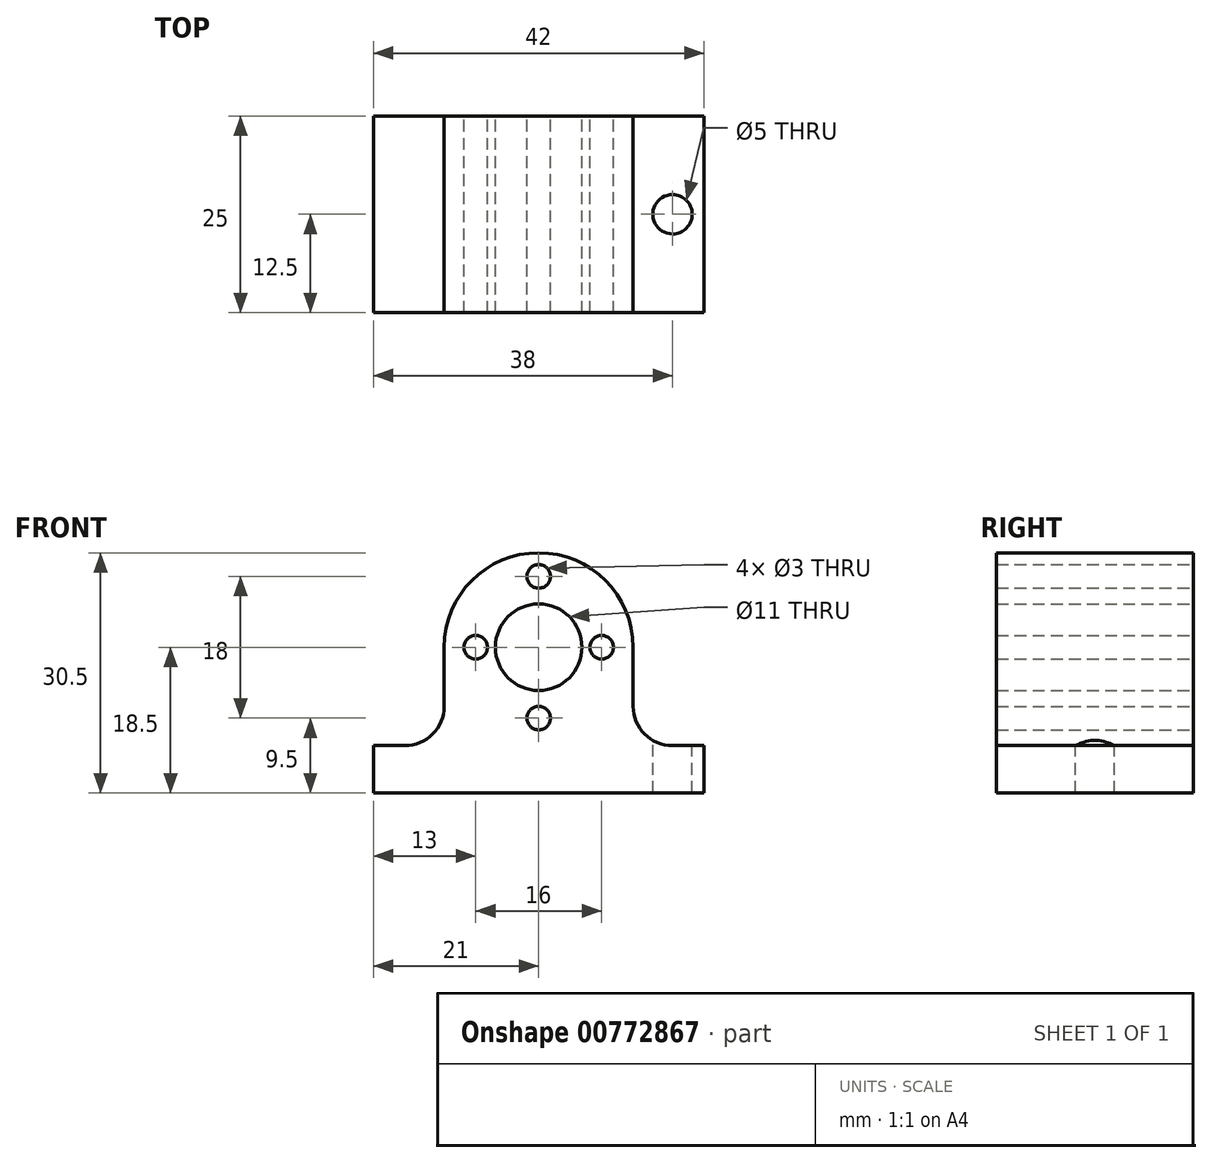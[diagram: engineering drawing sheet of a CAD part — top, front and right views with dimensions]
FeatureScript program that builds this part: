
annotation { "Feature Type Name" : "Feature", "Feature Type Description" : "" }
export const myFeature = defineFeature(function(context is Context, id is Id, definition is map)
    precondition{}
    {
        {
            var Q0;
            Q0=qCreatedBy(makeId("Front.planeOp"),FACE);
            var sketch = newSketch(context, id + "F0", { "sketchPlane" : qUnion([Q0])});
            skCircle(sketch, "E0", {"center": v(0, 0) * mm, "radius": 5.5 * mm});
            skCircle(sketch, "E1", {"center": v(0, 0) * mm, "radius": 12 * mm});
            skCircle(sketch, "E2", {"center": v(0, 9) * mm, "radius": 1.5 * mm});
            skCircle(sketch, "E3.MirrorC", {"center": v(0, -9) * mm, "radius": 1.5 * mm});
            skCircle(sketch, "E4.MirrorC", {"center": v(-8, 0) * mm, "radius": 1.5 * mm});
            skCircle(sketch, "E5.MirrorC", {"center": v(8, 0) * mm, "radius": 1.5 * mm});
            skLineSegment(sketch, "E6", {"start": v(-12, -12.5) * mm, "end": v(-21, -12.5) * mm});
            skLineSegment(sketch, "E7", {"start": v(-21, -12.5) * mm, "end": v(-21, -18.5) * mm});
            skLineSegment(sketch, "E8.MirrorCS", {"start": v(12, -12.5) * mm, "end": v(21, -12.5) * mm});
            skLineSegment(sketch, "E9.MirrorCS", {"start": v(21, -12.5) * mm, "end": v(21, -18.5) * mm});
            skLineSegment(sketch, "E10", {"start": v(-21, -18.5) * mm, "end": v(21, -18.5) * mm});
            skLineSegment(sketch, "E11", {"start": v(-12, 0) * mm, "end": v(-12, -12.5) * mm});
            skLineSegment(sketch, "E12", {"start": v(12, 0) * mm, "end": v(12, -12.5) * mm});
            skPoint(sketch, "E13.orphan", {"position": v(11, -12.5) * mm});
            skPoint(sketch, "E14.orphan", {"position": v(-11, -12.5) * mm});
            skSolve(sketch);
        }
        {
            var Q0;
            Q0 = qSketchRegion(id + "F0", true);
            extrude(context, id + "F1", {"entities" : qUnion([Q0]), "depth" : 25 * mm, "offsetDistance" : 25 * mm});
        }
        {
            var Q0;
            Q0=makeQuery(id+"F1.opExtrude","SWEPT_FACE",FACE,{"disambiguationData":[OSD([sQuery(id+"F0.wireOp",EDGE,"E8.MirrorCS")])]});
            var sketch = newSketch(context, id + "F2", { "sketchPlane" : qUnion([Q0])});
            skCircle(sketch, "E15", {"center": v(17, -12.5) * mm, "radius": 2.5 * mm});
            skCircle(sketch, "E16.MirrorC", {"center": v(-17, -12.5) * mm, "radius": 2.5 * mm});
            skSolve(sketch);
        }
        {
            var Q0;
            Q0=makeQuery(id+"F2.imprint","IMPRINT",FACE,{"disambiguationData":[TD([[makeQuery(id+"F2.imprint","IMPRINT",EDGE,{"derivedFrom":sQuery(id+"F2.wireOp",EDGE,"E15")}),1.0]])]});
            var Q1;
            Q1=makeQuery(id+"F2.imprint","IMPRINT",FACE,{"disambiguationData":[TD([[makeQuery(id+"F2.imprint","IMPRINT",EDGE,{"derivedFrom":sQuery(id+"F2.wireOp",EDGE,"c6ebee95-956a-4f15-aef1-c8e1f02ef2970.MirrorC")}),-1.0]])]});
            var Q2;
            Q2=makeQuery(id+"F2.imprint","IMPRINT",FACE,{"disambiguationData":[TD([[makeQuery(id+"F2.imprint","IMPRINT",EDGE,{"derivedFrom":sQuery(id+"F2.wireOp",EDGE,"E16.MirrorC")}),-1.0]])]});
            extrude(context, id + "F3", {"entities" : qUnion([Q0, Q1, Q2]), "operationType" : NewBodyOperationType.REMOVE, "endBound" : BoundingType.THROUGH_ALL, "oppositeDirection" : true, "depth" : 25 * mm, "offsetDistance" : 25 * mm});
        }
        {
            var Q0;
            Q0=makeQuery(id+"F1.opExtrude","SWEPT_EDGE",EDGE,{"disambiguationData":[OSD([sQuery(id+"F0.wireOp",EDGE,"E8.MirrorCS"),sQuery(id+"F0.wireOp",EDGE,"E12")])]});
            var Q1;
            Q1=makeQuery(id+"F1.opExtrude","SWEPT_EDGE",EDGE,{"disambiguationData":[OSD([sQuery(id+"F0.wireOp",EDGE,"E6"),sQuery(id+"F0.wireOp",EDGE,"E11")])]});
            fillet(context, id + "F4", {"entities" : qUnion([Q0, Q1]), "radius" : 5 * mm, "tangentPropagation" : true, "allowEdgeOverflow" : false});
        }
    });
